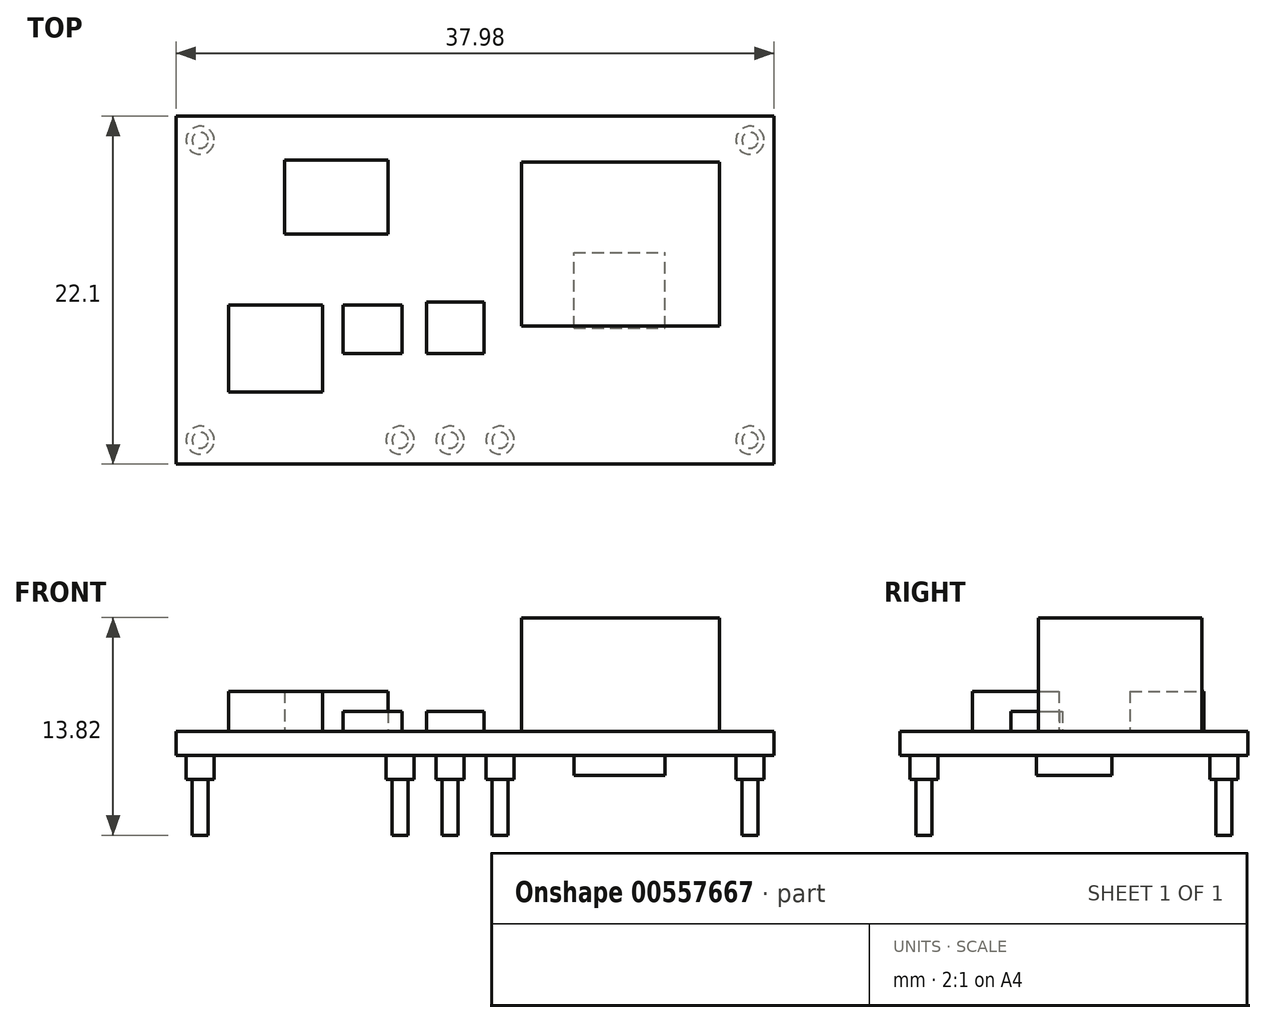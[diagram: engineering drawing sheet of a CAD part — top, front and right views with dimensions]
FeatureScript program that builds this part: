
annotation { "Feature Type Name" : "Feature", "Feature Type Description" : "" }
export const myFeature = defineFeature(function(context is Context, id is Id, definition is map)
    precondition{}
    {
        {
            var Q0;
            Q0=qCreatedBy(makeId("Top.planeOp"),FACE);
            var sketch = newSketch(context, id + "F0", { "sketchPlane" : qUnion([Q0])});
            skLineSegment(sketch, "E0.bottom", {"start": v(18.99, -11.05) * mm, "end": v(-18.99, -11.05) * mm});
            skLineSegment(sketch, "E0.top", {"start": v(18.99, 11.05) * mm, "end": v(-18.99, 11.05) * mm});
            skLineSegment(sketch, "E0.left", {"start": v(18.99, -11.05) * mm, "end": v(18.99, 11.05) * mm});
            skLineSegment(sketch, "E0.right", {"start": v(-18.99, -11.05) * mm, "end": v(-18.99, 11.05) * mm});
            skPoint(sketch, "E0.middle", {"position": v(0, 0) * mm});
            skSolve(sketch);
        }
        {
            var Q0;
            Q0 = qSketchRegion(id + "F0", true);
            extrude(context, id + "F1", {"entities" : qUnion([Q0]), "depth" : 1.52 * mm, "offsetDistance" : 25.4 * mm});
        }
        {
            var Q0;
            Q0=makeQuery(id+"F1.opExtrude","CAP_FACE",FACE,{"disambiguationData":[OSD([sQuery(id+"F0.wireOp",EDGE,"E0.bottom"),sQuery(id+"F0.wireOp",EDGE,"E0.top"),sQuery(id+"F0.wireOp",EDGE,"E0.left"),sQuery(id+"F0.wireOp",EDGE,"E0.right")])],"isStart":false});
            var sketch = newSketch(context, id + "F2", { "sketchPlane" : qUnion([Q0])});
            skLineSegment(sketch, "E1.bottom", {"start": v(15.5, -2.27) * mm, "end": v(2.94, -2.27) * mm});
            skLineSegment(sketch, "E1.top", {"start": v(15.5, 8.12) * mm, "end": v(2.94, 8.12) * mm});
            skLineSegment(sketch, "E1.left", {"start": v(15.5, -2.27) * mm, "end": v(15.5, 8.12) * mm});
            skLineSegment(sketch, "E1.right", {"start": v(2.94, -2.27) * mm, "end": v(2.94, 8.12) * mm});
            skPoint(sketch, "E1.middle", {"position": v(9.23, 2.93) * mm});
            skSolve(sketch);
        }
        {
            var Q0;
            Q0 = qSketchRegion(id + "F2", true);
            extrude(context, id + "F3", {"entities" : qUnion([Q0]), "depth" : 7.2 * mm, "offsetDistance" : 25.4 * mm});
        }
        {
            var Q0;
            Q0=makeQuery(id+"F1.opExtrude","CAP_FACE",FACE,{"disambiguationData":[OSD([sQuery(id+"F0.wireOp",EDGE,"E0.bottom"),sQuery(id+"F0.wireOp",EDGE,"E0.top"),sQuery(id+"F0.wireOp",EDGE,"E0.left"),sQuery(id+"F0.wireOp",EDGE,"E0.right")])],"isStart":false});
            var sketch = newSketch(context, id + "F4", { "sketchPlane" : qUnion([Q0])});
            skLineSegment(sketch, "E2.bottom", {"start": v(-5.53, 3.56) * mm, "end": v(-12.09, 3.56) * mm});
            skLineSegment(sketch, "E2.top", {"start": v(-5.53, 8.25) * mm, "end": v(-12.09, 8.25) * mm});
            skLineSegment(sketch, "E2.left", {"start": v(-5.53, 3.56) * mm, "end": v(-5.53, 8.25) * mm});
            skLineSegment(sketch, "E2.right", {"start": v(-12.09, 3.56) * mm, "end": v(-12.09, 8.25) * mm});
            skPoint(sketch, "E2.middle", {"position": v(-8.8, 5.9) * mm});
            skLineSegment(sketch, "E3.bottom", {"start": v(-9.68, -6.46) * mm, "end": v(-15.67, -6.46) * mm});
            skLineSegment(sketch, "E3.top", {"start": v(-9.68, -0.95) * mm, "end": v(-15.67, -0.95) * mm});
            skLineSegment(sketch, "E3.left", {"start": v(-9.68, -6.46) * mm, "end": v(-9.68, -0.95) * mm});
            skLineSegment(sketch, "E3.right", {"start": v(-15.67, -6.46) * mm, "end": v(-15.67, -0.95) * mm});
            skPoint(sketch, "E3.middle", {"position": v(-12.67, -3.7) * mm});
            skSolve(sketch);
        }
        {
            var Q0;
            Q0 = qSketchRegion(id + "F4", true);
            extrude(context, id + "F5", {"entities" : qUnion([Q0]), "depth" : 2.54 * mm, "offsetDistance" : 25.4 * mm});
        }
        {
            var Q0;
            Q0=makeQuery(id+"F1.opExtrude","CAP_FACE",FACE,{"disambiguationData":[OSD([sQuery(id+"F0.wireOp",EDGE,"E0.bottom"),sQuery(id+"F0.wireOp",EDGE,"E0.top"),sQuery(id+"F0.wireOp",EDGE,"E0.left"),sQuery(id+"F0.wireOp",EDGE,"E0.right")])],"isStart":false});
            var sketch = newSketch(context, id + "F6", { "sketchPlane" : qUnion([Q0])});
            skLineSegment(sketch, "E4.bottom", {"start": v(-4.64, -4.02) * mm, "end": v(-8.38, -4.02) * mm});
            skLineSegment(sketch, "E4.top", {"start": v(-4.64, -0.94) * mm, "end": v(-8.38, -0.94) * mm});
            skLineSegment(sketch, "E4.left", {"start": v(-4.64, -4.02) * mm, "end": v(-4.64, -0.94) * mm});
            skLineSegment(sketch, "E4.right", {"start": v(-8.38, -4.02) * mm, "end": v(-8.38, -0.94) * mm});
            skPoint(sketch, "E4.middle", {"position": v(-6.5, -2.48) * mm});
            skLineSegment(sketch, "E5.bottom", {"start": v(0.56, -4.02) * mm, "end": v(-3.08, -4.02) * mm});
            skLineSegment(sketch, "E5.top", {"start": v(0.56, -0.74) * mm, "end": v(-3.08, -0.74) * mm});
            skLineSegment(sketch, "E5.left", {"start": v(0.56, -4.02) * mm, "end": v(0.56, -0.74) * mm});
            skLineSegment(sketch, "E5.right", {"start": v(-3.08, -4.02) * mm, "end": v(-3.08, -0.74) * mm});
            skPoint(sketch, "E5.middle", {"position": v(-1.26, -2.38) * mm});
            skSolve(sketch);
        }
        {
            var Q0;
            Q0 = qSketchRegion(id + "F6", true);
            extrude(context, id + "F7", {"entities" : qUnion([Q0]), "depth" : 1.27 * mm, "offsetDistance" : 25.4 * mm});
        }
        {
            var Q0;
            Q0=makeQuery(id+"F1.opExtrude","CAP_FACE",FACE,{"disambiguationData":[OSD([sQuery(id+"F0.wireOp",EDGE,"E0.bottom"),sQuery(id+"F0.wireOp",EDGE,"E0.top"),sQuery(id+"F0.wireOp",EDGE,"E0.left"),sQuery(id+"F0.wireOp",EDGE,"E0.right")])],"isStart":true});
            var sketch = newSketch(context, id + "F8", { "sketchPlane" : qUnion([Q0])});
            skLineSegment(sketch, "E6.bottom", {"start": v(6.27, 2.4) * mm, "end": v(12.05, 2.4) * mm});
            skLineSegment(sketch, "E6.top", {"start": v(6.27, -2.4) * mm, "end": v(12.05, -2.4) * mm});
            skLineSegment(sketch, "E6.left", {"start": v(6.27, 2.4) * mm, "end": v(6.27, -2.4) * mm});
            skLineSegment(sketch, "E6.right", {"start": v(12.05, 2.4) * mm, "end": v(12.05, -2.4) * mm});
            skPoint(sketch, "E6.middle", {"position": v(9.16, 0) * mm});
            skSolve(sketch);
        }
        {
            var Q0;
            Q0 = qSketchRegion(id + "F8", true);
            extrude(context, id + "F9", {"entities" : qUnion([Q0]), "depth" : 1.27 * mm, "offsetDistance" : 25.4 * mm});
        }
        {
            var Q0;
            Q0=makeQuery(id+"F1.opExtrude","CAP_FACE",FACE,{"disambiguationData":[OSD([sQuery(id+"F0.wireOp",EDGE,"E0.bottom"),sQuery(id+"F0.wireOp",EDGE,"E0.top"),sQuery(id+"F0.wireOp",EDGE,"E0.left"),sQuery(id+"F0.wireOp",EDGE,"E0.right")])],"isStart":true});
            var sketch = newSketch(context, id + "F10", { "sketchPlane" : qUnion([Q0])});
            skCircle(sketch, "E7", {"center": v(17.46, -9.52) * mm, "radius": 0.89 * mm});
            skCircle(sketch, "E8", {"center": v(-17.46, -9.53) * mm, "radius": 0.89 * mm});
            skCircle(sketch, "E9", {"center": v(-17.46, 9.52) * mm, "radius": 0.89 * mm});
            skCircle(sketch, "E10", {"center": v(-4.76, 9.52) * mm, "radius": 0.89 * mm});
            skCircle(sketch, "E11", {"center": v(-1.59, 9.52) * mm, "radius": 0.89 * mm});
            skCircle(sketch, "E12", {"center": v(1.59, 9.52) * mm, "radius": 0.89 * mm});
            skCircle(sketch, "E13", {"center": v(17.46, 9.52) * mm, "radius": 0.89 * mm});
            skLineSegment(sketch, "E14", {"start": v(-17.46, -9.53) * mm, "end": v(-17.46, 9.52) * mm, "construction": true});
            skLineSegment(sketch, "E15", {"start": v(-17.46, 9.52) * mm, "end": v(17.46, 9.52) * mm, "construction": true});
            skLineSegment(sketch, "E16", {"start": v(17.46, 9.52) * mm, "end": v(17.46, -9.52) * mm, "construction": true});
            skSolve(sketch);
        }
        {
            var Q0;
            Q0 = qSketchRegion(id + "F10", true);
            extrude(context, id + "F11", {"entities" : qUnion([Q0]), "depth" : 1.52 * mm, "offsetDistance" : 25.4 * mm});
        }
        {
            var Q0;
            Q0=makeQuery(id+"F11.opExtrude","CAP_FACE",FACE,{"disambiguationData":[OSD([sQuery(id+"F10.wireOp",EDGE,"E12")])],"isStart":false});
            var sketch = newSketch(context, id + "F12", { "sketchPlane" : qUnion([Q0])});
            skCircle(sketch, "E17", {"center": v(-17.46, -9.52) * mm, "radius": 0.5 * mm});
            skCircle(sketch, "E18", {"center": v(-17.46, 9.53) * mm, "radius": 0.5 * mm});
            skCircle(sketch, "E19", {"center": v(-4.76, 9.53) * mm, "radius": 0.5 * mm});
            skCircle(sketch, "E20", {"center": v(-1.59, 9.53) * mm, "radius": 0.5 * mm});
            skCircle(sketch, "E21", {"center": v(1.59, 9.52) * mm, "radius": 0.5 * mm});
            skCircle(sketch, "E22", {"center": v(17.46, 9.53) * mm, "radius": 0.5 * mm});
            skCircle(sketch, "E23", {"center": v(17.46, -9.52) * mm, "radius": 0.5 * mm});
            skLineSegment(sketch, "E24", {"start": v(-17.46, -9.52) * mm, "end": v(-17.46, 9.53) * mm, "construction": true});
            skLineSegment(sketch, "E25", {"start": v(-17.46, 9.53) * mm, "end": v(17.46, 9.53) * mm, "construction": true});
            skLineSegment(sketch, "E26", {"start": v(17.46, 9.53) * mm, "end": v(17.46, -9.52) * mm, "construction": true});
            skSolve(sketch);
        }
        {
            var Q0;
            Q0 = qSketchRegion(id + "F12", true);
            extrude(context, id + "F13", {"entities" : qUnion([Q0]), "depth" : 3.56 * mm, "offsetDistance" : 25.4 * mm});
        }
    });
